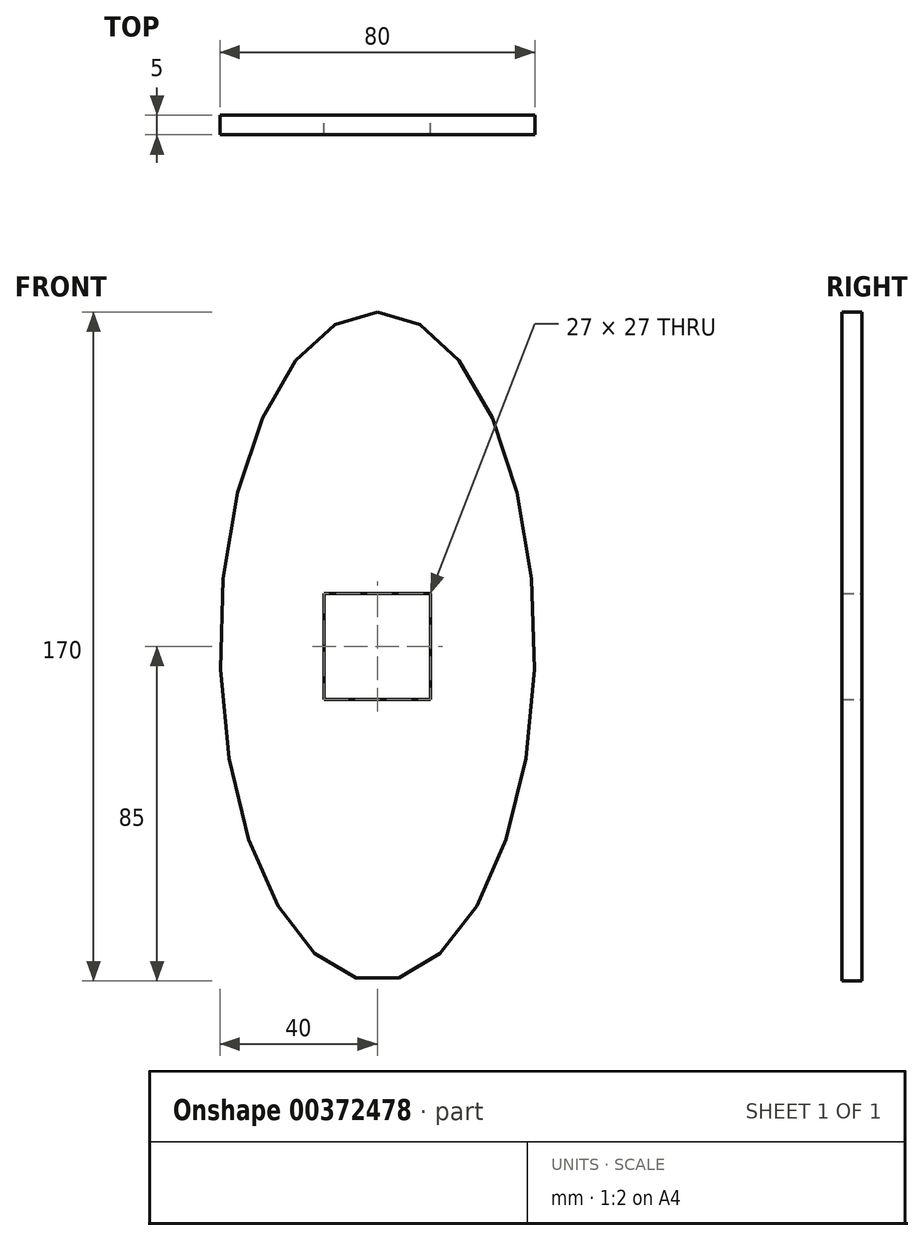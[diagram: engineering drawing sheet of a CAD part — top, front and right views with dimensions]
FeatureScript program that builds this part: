
annotation { "Feature Type Name" : "Feature", "Feature Type Description" : "" }
export const myFeature = defineFeature(function(context is Context, id is Id, definition is map)
    precondition{}
    {
        {
            var Q0;
            Q0=qCreatedBy(makeId("Front.planeOp"),FACE);
            var sketch = newSketch(context, id + "F0", { "sketchPlane" : qUnion([Q0])});
            skLineSegment(sketch, "E0.bottom", {"start": v(0, 0) * mm, "end": v(27, 0) * mm});
            skLineSegment(sketch, "E0.top", {"start": v(0, 27) * mm, "end": v(27, 27) * mm});
            skLineSegment(sketch, "E0.left", {"start": v(0, 0) * mm, "end": v(0, 27) * mm});
            skLineSegment(sketch, "E0.right", {"start": v(27, 0) * mm, "end": v(27, 27) * mm});
            skEllipse(sketch, "E1", {"center": v(13.5, 13.5) * mm, "majorRadius": 85 * mm, "minorRadius": 40 * mm, "majorAxis": v(0, 1)});
            skPoint(sketch, "E1.centerSnap0", {"position": v(27, 13.5) * mm});
            skPoint(sketch, "E1.centerSnap1", {"position": v(13.5, 27) * mm});
            skLineSegment(sketch, "E2", {"start": v(13.5, 98.5) * mm, "end": v(13.5, 13.5) * mm});
            skPoint(sketch, "E2.startSnap0", {"position": v(13.5, 98.5) * mm});
            skLineSegment(sketch, "E3", {"start": v(13.5, 13.5) * mm, "end": v(53.5, 13.5) * mm});
            skSolve(sketch);
        }
        {
            var Q0;
            {var subQ3=sQuery(id+"F0.wireOp",EDGE,"E0.top");var subQ5=sQuery(id+"F0.wireOp",EDGE,"E0.right");var subQ6=makeQuery(id+"F0.imprint","INTERSECT",VERTEX,{"derivedFrom":[subQ3,subQ5]});Q0=makeQuery(id+"F0.imprint","IMPRINT",FACE,{"disambiguationData":[TD([[makeQuery(id+"F0.imprint","IMPRINT",EDGE,{"disambiguationData":[TD([[subQ6,1.0]])],"derivedFrom":subQ3}),1.0]])]});}
            var sketch = newSketch(context, id + "F1", { "sketchPlane" : qUnion([Q0])});
            skSolve(sketch);
        }
        {
            var Q0;
            Q0 = qSketchRegion(id + "F1", true);
            var Q1;
            {var subQ1=sQuery(id+"F0.wireOp",EDGE,"E0.bottom");Q1=makeQuery(id+"F0.imprint","IMPRINT",FACE,{"disambiguationData":[TD([[makeQuery(id+"F0.imprint","IMPRINT",EDGE,{"derivedFrom":subQ1}),-1.0]])]});}
            var Q2;
            {var subQ3=sQuery(id+"F0.wireOp",EDGE,"E0.top");var subQ5=sQuery(id+"F0.wireOp",EDGE,"E0.right");var subQ6=makeQuery(id+"F0.imprint","INTERSECT",VERTEX,{"derivedFrom":[subQ3,subQ5]});Q2=makeQuery(id+"F0.imprint","IMPRINT",FACE,{"disambiguationData":[TD([[makeQuery(id+"F0.imprint","IMPRINT",EDGE,{"disambiguationData":[TD([[subQ6,1.0]])],"derivedFrom":subQ3}),1.0]])]});}
            extrude(context, id + "F2", {"entities" : qUnion([Q0, Q1, Q2]), "depth" : 5 * mm});
        }
    });
